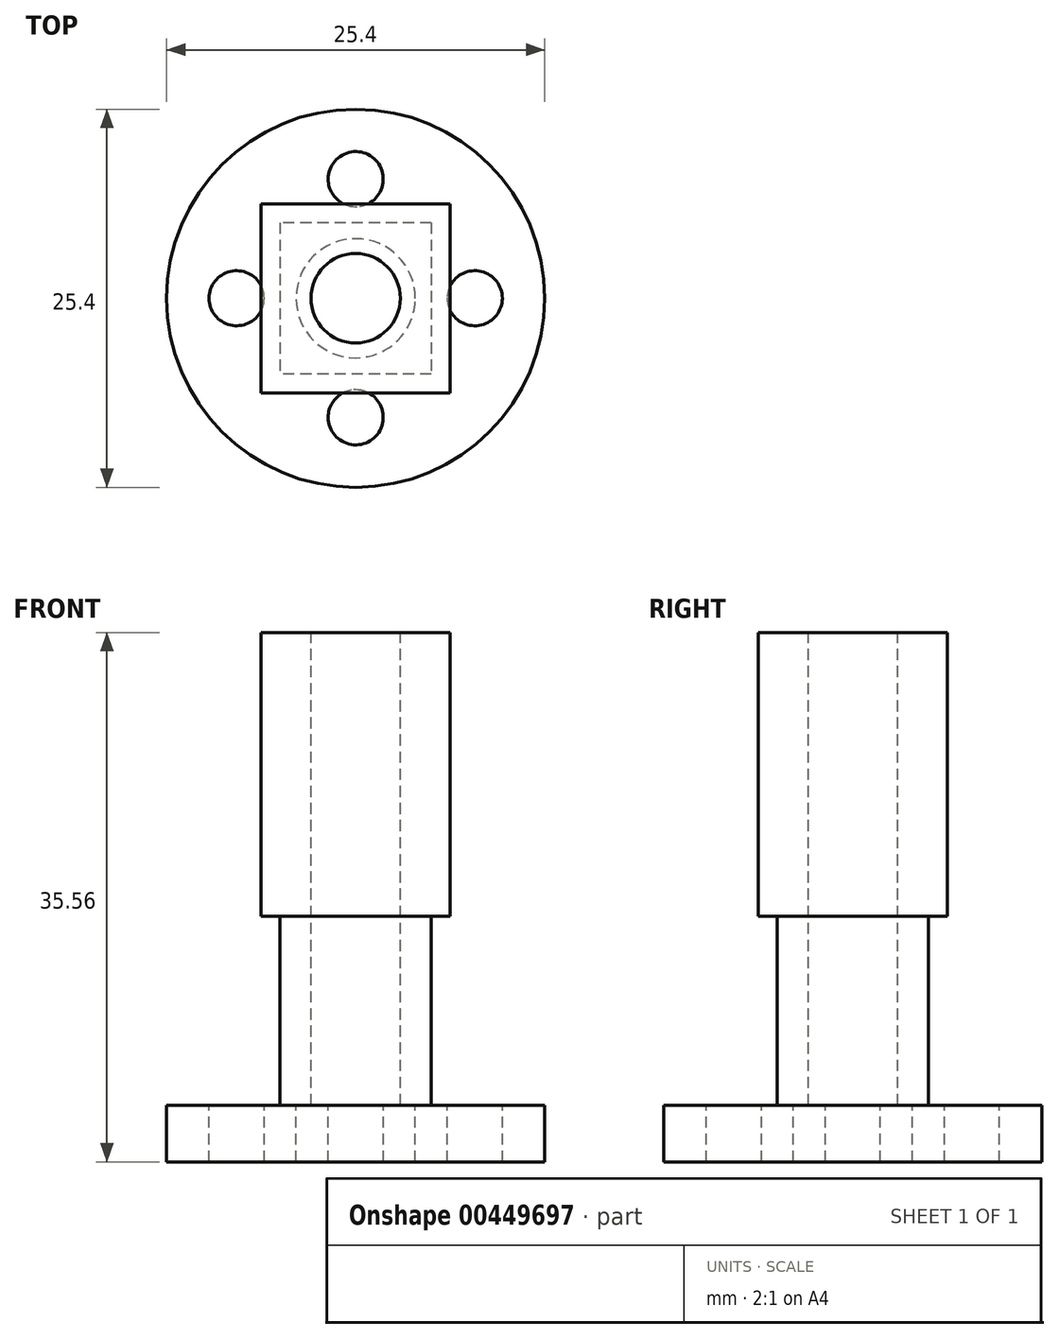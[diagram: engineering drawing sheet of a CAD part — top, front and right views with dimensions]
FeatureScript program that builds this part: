
annotation { "Feature Type Name" : "Feature", "Feature Type Description" : "" }
export const myFeature = defineFeature(function(context is Context, id is Id, definition is map)
    precondition{}
    {
        {
            var Q0;
            Q0=qCreatedBy(makeId("Top.planeOp"),FACE);
            var sketch = newSketch(context, id + "F0", { "sketchPlane" : qUnion([Q0])});
            skLineSegment(sketch, "E0.bottom", {"start": v(0, 0) * mm, "end": v(-12.7, 0) * mm});
            skLineSegment(sketch, "E0.top", {"start": v(0, 12.7) * mm, "end": v(-12.7, 12.7) * mm});
            skLineSegment(sketch, "E0.left", {"start": v(0, 0) * mm, "end": v(0, 12.7) * mm});
            skLineSegment(sketch, "E0.right", {"start": v(-12.7, 0) * mm, "end": v(-12.7, 12.7) * mm});
            skSolve(sketch);
        }
        {
            var Q0;
            Q0=makeQuery(id+"F0.imprint","IMPRINT",FACE,{"disambiguationData":[TD([[makeQuery(id+"F0.imprint","IMPRINT",EDGE,{"derivedFrom":sQuery(id+"F0.wireOp",EDGE,"E0.bottom")}),-1.0]])]});
            extrude(context, id + "F1", {"entities" : qUnion([Q0]), "depth" : 19.05 * mm});
        }
        {
            var Q0;
            Q0=makeQuery(id+"F1.opExtrude","CAP_FACE",FACE,{"disambiguationData":[OSD([sQuery(id+"F0.wireOp",EDGE,"E0.bottom"),sQuery(id+"F0.wireOp",EDGE,"E0.top"),sQuery(id+"F0.wireOp",EDGE,"E0.left"),sQuery(id+"F0.wireOp",EDGE,"E0.right")])],"isStart":true});
            var sketch = newSketch(context, id + "F2", { "sketchPlane" : qUnion([Q0])});
            skLineSegment(sketch, "E1.bottom", {"start": v(-1.27, -11.43) * mm, "end": v(-11.43, -11.43) * mm});
            skLineSegment(sketch, "E1.top", {"start": v(-1.27, -1.27) * mm, "end": v(-11.43, -1.27) * mm});
            skLineSegment(sketch, "E1.left", {"start": v(-1.27, -11.43) * mm, "end": v(-1.27, -1.27) * mm});
            skLineSegment(sketch, "E1.right", {"start": v(-11.43, -11.43) * mm, "end": v(-11.43, -1.27) * mm});
            skPoint(sketch, "E1.middle", {"position": v(-6.35, -6.35) * mm});
            skPoint(sketch, "E1.middle.positionSnap0", {"position": v(0, -6.35) * mm});
            skPoint(sketch, "E1.middle.positionSnap1", {"position": v(-6.35, -12.7) * mm});
            skPoint(sketch, "E1.centerSnap0", {"position": v(0, -6.35) * mm});
            skPoint(sketch, "E1.centerSnap1", {"position": v(-6.35, -12.7) * mm});
            skCircle(sketch, "E2", {"center": v(-6.35, -6.35) * mm, "radius": 3 * mm});
            skSolve(sketch);
        }
        {
            var Q0;
            Q0 = qSketchRegion(id + "F2", true);
            extrude(context, id + "F3", {"entities" : qUnion([Q0]), "operationType" : NewBodyOperationType.ADD, "depth" : 12.7 * mm});
        }
        {
            var Q0;
            Q0=makeQuery(id+"F3.opExtrude","CAP_FACE",FACE,{"disambiguationData":[OSD([sQuery(id+"F2.wireOp",EDGE,"E1.bottom"),sQuery(id+"F2.wireOp",EDGE,"E1.top"),sQuery(id+"F2.wireOp",EDGE,"E1.left"),sQuery(id+"F2.wireOp",EDGE,"E1.right")])],"isStart":false});
            var sketch = newSketch(context, id + "F4", { "sketchPlane" : qUnion([Q0])});
            skCircle(sketch, "E3", {"center": v(-6.35, -6.35) * mm, "radius": 12.7 * mm});
            skPoint(sketch, "E3.centerSnap0", {"position": v(-1.27, -6.35) * mm});
            skPoint(sketch, "E3.centerSnap1", {"position": v(-6.35, -11.43) * mm});
            skCircle(sketch, "E4", {"center": v(-6.35, -6.35) * mm, "radius": 4 * mm});
            skCircle(sketch, "E5", {"center": v(-6.35, -14.35) * mm, "radius": 1.85 * mm});
            skCircle(sketch, "E6.1.0", {"center": v(1.65, -6.35) * mm, "radius": 1.85 * mm});
            skCircle(sketch, "E6.2.0", {"center": v(-6.35, 1.65) * mm, "radius": 1.85 * mm});
            skCircle(sketch, "E6.3.0", {"center": v(-14.35, -6.35) * mm, "radius": 1.85 * mm});
            skSolve(sketch);
        }
        {
            var Q0;
            Q0=makeQuery(id+"F4.imprint","IMPRINT",FACE,{"disambiguationData":[TD([[makeQuery(id+"F4.imprint","IMPRINT",EDGE,{"derivedFrom":sQuery(id+"F4.wireOp",EDGE,"E3")}),1.0]])]});
            var Q1;
            Q1=makeQuery(id+"F4.imprint","IMPRINT",FACE,{"disambiguationData":[TD([[makeQuery(id+"F4.imprint","IMPRINT",EDGE,{"derivedFrom":sQuery(id+"F4.wireOp",EDGE,"E4")}),-1.0]])]});
            extrude(context, id + "F5", {"entities" : qUnion([Q0, Q1]), "depth" : 3.8 * mm});
        }
        {
            var Q0;
            Q0=makeQuery(id+"F3.boolean.opBoolean","SPLIT",FACE,{"disambiguationData":[TD([makeQuery(id+"F3.opExtrude","SWEPT_FACE",FACE,{"disambiguationData":[OSD([sQuery(id+"F2.wireOp",EDGE,"E2")])]})])],"derivedFrom":makeQuery(id+"F1.opExtrude","CAP_FACE",FACE,{"disambiguationData":[OSD([sQuery(id+"F0.wireOp",EDGE,"E0.bottom"),sQuery(id+"F0.wireOp",EDGE,"E0.top"),sQuery(id+"F0.wireOp",EDGE,"E0.left"),sQuery(id+"F0.wireOp",EDGE,"E0.right")])],"isStart":true})});
            extrude(context, id + "F6", {"entities" : qUnion([Q0]), "operationType" : NewBodyOperationType.REMOVE, "oppositeDirection" : true, "depth" : 127 * mm});
        }
    });
